# Revit family: Hand_Dryer-Excel_Dryer-Wall_Guard
name_source: partatom
category: Specialty Equipment
revit_build: Autodesk Revit 2015 (Build: 20140606_1530(x64)
units: mm (PartAtom-declared; Revit-internal decimal feet)

## types (3) — shared parameters
BIMobject category = Dryers (Hand & Hair)
Date of publishing = 3/6/2017
Default Elevation = 1' - 5 9/16"
Depth = 0' - 0 1/16"
Description = Wall Guard
Design country = United States
Edition number = 1
Height = 2' - 8"
IFC Classification = Furnishing Element
Manufacturer = Excel Dryer
Manufacturer country = United States
Manufacturer name = Excel Dryer US
Masterformat 2014 Code = 10 28 13.13
Masterformat 2014 Description = Commercial Toilet Accessories
Material main = Zink
Material secondary = Zink
Nominal height = 0' - 0"
Nominal width = 0' - 0"
OmniClass Code = 23-31 25 15
OmniClass Description = Hand Dryers
Product Documentation Link = http://www.exceldryer.com
Product Guid = 29c789c6-b5d6-4169-b2f0-1360146b7577
Product Page URL = http://www.exceldryer.com
Product SKU = excel_xlerator_wallguard
Product data url = https://bimobject.com
Product family = Equipment
Product group = Hand dryer
Product url = http://www.exceldryer.com
QR code = http://bimobject.com
UNSPSC Code = 301815
URL = http://www.exceldryer.com
Uniclass 1.4 Code = L721
Uniclass 1.4 Description = Sanitary equipment
Uniclass 2.0 Code = PR-31-75
Uniclass 2.0 Description = Sanitary Accessories
Uniclass 2015 Code = Pr_40_20_76
Uniclass 2015 Name = Sanitary accessories
Uniformat II Code = E1010
Uniformat II Description = Commercial Equipment
Weight Net (Kg) = 0
Width = 1' - 4"

## per-type parameters (varying)
| type | Model | Wall Guard Material |
| 89S | Wall Guard Stainless | Metal - Excel Dryer - Stainless Steel - Brushed |
| 89B | Wall Guard Black | Plastic - Excel Dryer - Anti-Microbial - Black |
| 89W | Wall Guard White | Plastic - Excel Dryer - Anti-Microbial - White |

## geometry (parser evidence)
native form markers: Sweep x3
no freeform markers — native parametric forms only
